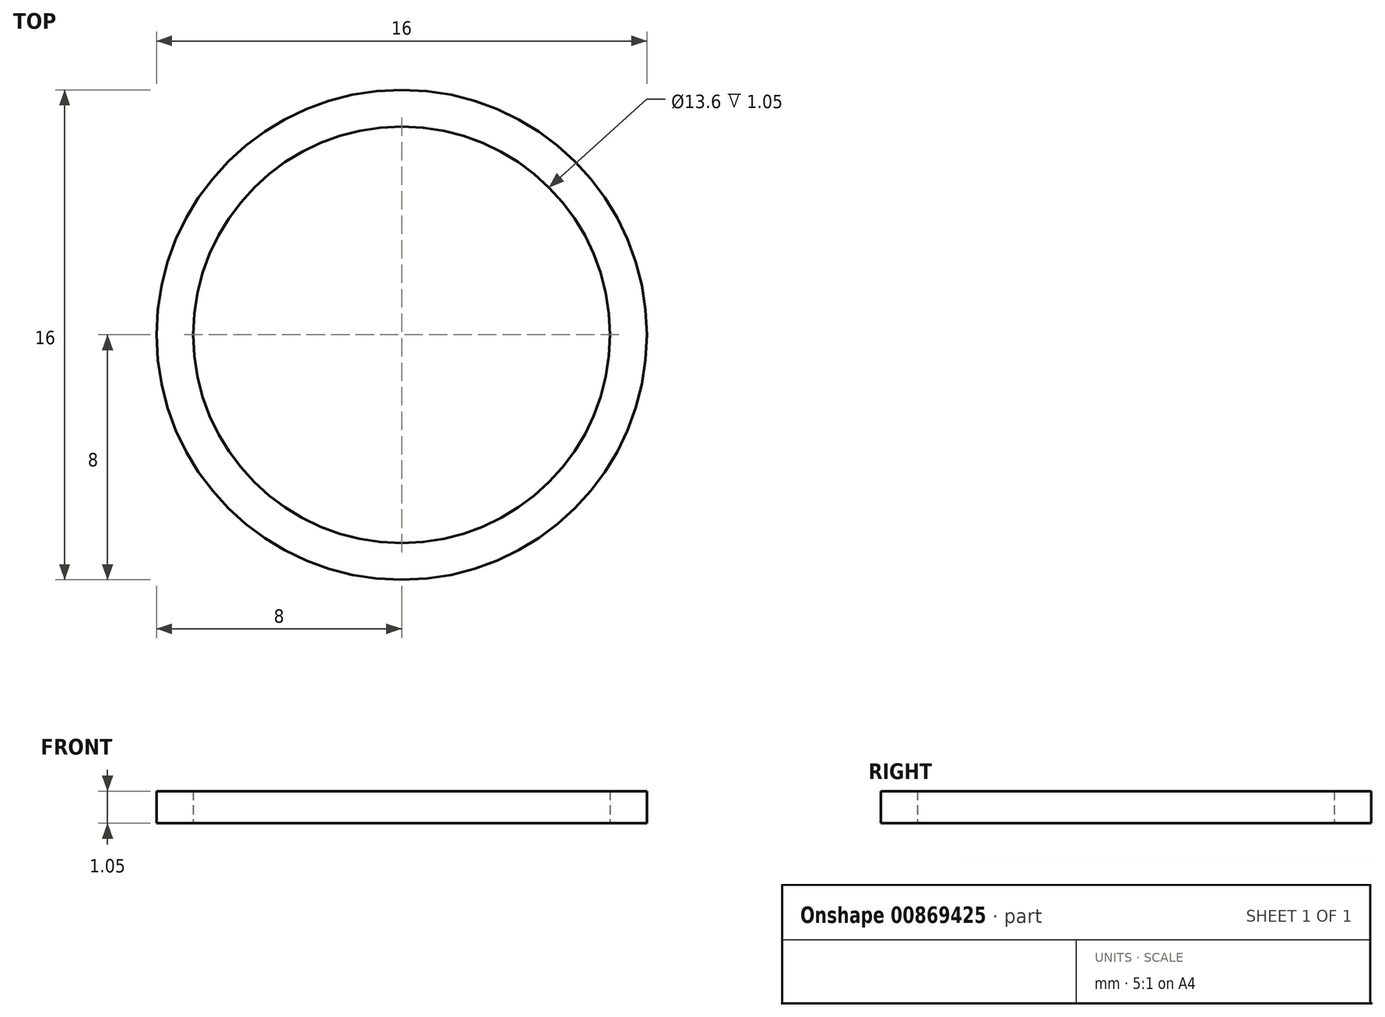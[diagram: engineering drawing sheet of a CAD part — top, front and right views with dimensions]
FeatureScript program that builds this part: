
annotation { "Feature Type Name" : "Feature", "Feature Type Description" : "" }
export const myFeature = defineFeature(function(context is Context, id is Id, definition is map)
    precondition{}
    {
        {
            var Q0;
            Q0=qCreatedBy(makeId("Top.planeOp"),FACE);
            var sketch = newSketch(context, id + "F0", { "sketchPlane" : qUnion([Q0])});
            skCircle(sketch, "E0", {"center": v(0, 0) * mm, "radius": 8 * mm});
            skCircle(sketch, "E1.0", {"center": v(0, 0) * mm, "radius": 6.8 * mm});
            skSolve(sketch);
        }
        {
            var Q0;
            Q0=makeQuery(id+"F0.imprint","IMPRINT",FACE,{"disambiguationData":[TD([[makeQuery(id+"F0.imprint","IMPRINT",EDGE,{"derivedFrom":sQuery(id+"F0.wireOp",EDGE,"E0")}),1.0]])]});
            extrude(context, id + "F1", {"entities" : qUnion([Q0]), "depth" : 1.05 * mm, "offsetDistance" : 25 * mm});
        }
    });
